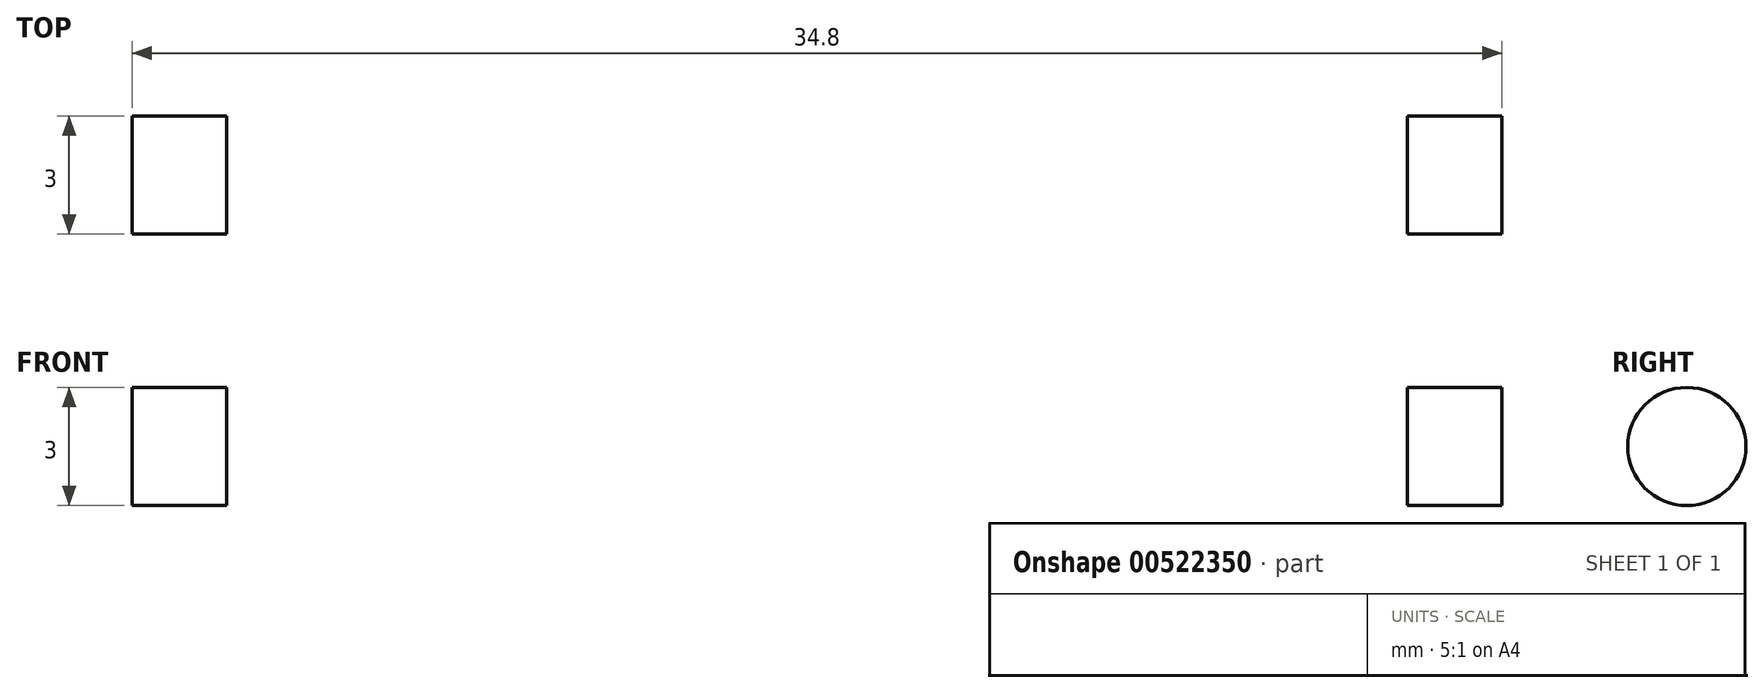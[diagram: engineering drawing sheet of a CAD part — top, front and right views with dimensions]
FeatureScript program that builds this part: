
annotation { "Feature Type Name" : "Feature", "Feature Type Description" : "" }
export const myFeature = defineFeature(function(context is Context, id is Id, definition is map)
    precondition{}
    {
        {
            var Q0;
            Q0=qCreatedBy(makeId("Top.planeOp"),FACE);
            var sketch = newSketch(context, id + "F0", { "sketchPlane" : qUnion([Q0])});
            skLineSegment(sketch, "E0.bottom", {"start": v(15, -21.5) * mm, "end": v(5, -21.5) * mm});
            skLineSegment(sketch, "E0.top", {"start": v(15, 21.5) * mm, "end": v(5, 21.5) * mm});
            skLineSegment(sketch, "E0.left", {"start": v(15, -21.5) * mm, "end": v(15, -5) * mm});
            skLineSegment(sketch, "E0.right", {"start": v(-15, -21.5) * mm, "end": v(-15, -5) * mm});
            skPoint(sketch, "E0.middle", {"position": v(0, 0) * mm});
            skLineSegment(sketch, "E1.bottom", {"start": v(5, -22.7) * mm, "end": v(-5, -22.7) * mm});
            skLineSegment(sketch, "E1.top", {"start": v(5, 22.7) * mm, "end": v(-5, 22.7) * mm});
            skLineSegment(sketch, "E1.left", {"start": v(16.2, -5) * mm, "end": v(16.2, 5) * mm});
            skLineSegment(sketch, "E1.right", {"start": v(-16.2, -5) * mm, "end": v(-16.2, 5) * mm});
            skLineSegment(sketch, "E2.bottom", {"start": v(17.4, -23.9) * mm, "end": v(-17.4, -23.9) * mm});
            skLineSegment(sketch, "E2.top", {"start": v(17.4, 23.9) * mm, "end": v(-17.4, 23.9) * mm});
            skLineSegment(sketch, "E2.left", {"start": v(17.4, -23.9) * mm, "end": v(17.4, 23.9) * mm});
            skLineSegment(sketch, "E2.right", {"start": v(-17.4, -23.9) * mm, "end": v(-17.4, 23.9) * mm});
            skLineSegment(sketch, "E3", {"start": v(-5, -21.5) * mm, "end": v(-5, -22.7) * mm});
            skLineSegment(sketch, "E4", {"start": v(5, -21.5) * mm, "end": v(5, -22.7) * mm});
            skLineSegment(sketch, "E5", {"start": v(0, 0) * mm, "end": v(0, -7.04) * mm, "construction": true});
            skLineSegment(sketch, "E6", {"start": v(-16.2, 5) * mm, "end": v(-15, 5) * mm});
            skLineSegment(sketch, "E7", {"start": v(-16.2, -5) * mm, "end": v(-15, -5) * mm});
            skLineSegment(sketch, "E8", {"start": v(0, 0) * mm, "end": v(8.38, 0) * mm, "construction": true});
            skLineSegment(sketch, "E9", {"start": v(15, 5) * mm, "end": v(16.2, 5) * mm});
            skLineSegment(sketch, "E10", {"start": v(15, -5) * mm, "end": v(16.2, -5) * mm});
            skLineSegment(sketch, "E11", {"start": v(-5, 22.7) * mm, "end": v(-5, 21.5) * mm});
            skLineSegment(sketch, "E12", {"start": v(5, 22.7) * mm, "end": v(5, 21.5) * mm});
            skLineSegment(sketch, "E13.trimOffspring", {"start": v(-5, 21.5) * mm, "end": v(-15, 21.5) * mm});
            skLineSegment(sketch, "E14.trimOffspring", {"start": v(-15, 5) * mm, "end": v(-15, 21.5) * mm});
            skLineSegment(sketch, "E15.trimOffspring", {"start": v(15, 5) * mm, "end": v(15, 21.5) * mm});
            skLineSegment(sketch, "E16.trimOffspring", {"start": v(-5, -21.5) * mm, "end": v(-15, -21.5) * mm});
            skPoint(sketch, "E17.orphan", {"position": v(-16.2, 22.7) * mm});
            skPoint(sketch, "E18.orphan", {"position": v(16.2, 22.7) * mm});
            skPoint(sketch, "E19.orphan", {"position": v(16.2, -22.7) * mm});
            skPoint(sketch, "E20.orphan", {"position": v(-16.2, -22.7) * mm});
            skLineSegment(sketch, "E21", {"start": v(5, 22.7) * mm, "end": v(5, 23.9) * mm});
            skLineSegment(sketch, "E22", {"start": v(-5, 22.7) * mm, "end": v(-5, 23.9) * mm});
            skLineSegment(sketch, "E23", {"start": v(16.2, 5) * mm, "end": v(17.4, 5) * mm});
            skLineSegment(sketch, "E24", {"start": v(16.2, -5) * mm, "end": v(17.4, -5) * mm});
            skLineSegment(sketch, "E25", {"start": v(-16.2, 5) * mm, "end": v(-17.4, 5) * mm});
            skLineSegment(sketch, "E26", {"start": v(-16.2, -5) * mm, "end": v(-17.4, -5) * mm});
            skLineSegment(sketch, "E27", {"start": v(-5, -22.7) * mm, "end": v(-5, -23.9) * mm});
            skLineSegment(sketch, "E28", {"start": v(5, -22.7) * mm, "end": v(5, -23.9) * mm});
            skSolve(sketch);
        }
        {
            var Q0;
            Q0=makeQuery(id+"F0.imprint","IMPRINT",FACE,{"disambiguationData":[TD([[makeQuery(id+"F0.imprint","IMPRINT",EDGE,{"derivedFrom":sQuery(id+"F0.wireOp",EDGE,"E0.bottom")}),1.0]])]});
            var Q1;
            Q1=makeQuery(id+"F0.imprint","IMPRINT",FACE,{"disambiguationData":[TD([[makeQuery(id+"F0.imprint","IMPRINT",EDGE,{"derivedFrom":sQuery(id+"F0.wireOp",EDGE,"E1.left")}),-1.0]])]});
            var Q2;
            Q2=makeQuery(id+"F0.imprint","IMPRINT",FACE,{"disambiguationData":[TD([[makeQuery(id+"F0.imprint","IMPRINT",EDGE,{"derivedFrom":sQuery(id+"F0.wireOp",EDGE,"E0.top")}),-1.0]])]});
            var Q3;
            Q3=makeQuery(id+"F0.imprint","IMPRINT",FACE,{"disambiguationData":[TD([[makeQuery(id+"F0.imprint","IMPRINT",EDGE,{"derivedFrom":sQuery(id+"F0.wireOp",EDGE,"E1.top")}),-1.0]])]});
            var Q4;
            Q4=makeQuery(id+"F0.imprint","IMPRINT",FACE,{"disambiguationData":[TD([[makeQuery(id+"F0.imprint","IMPRINT",EDGE,{"derivedFrom":sQuery(id+"F0.wireOp",EDGE,"E6")}),1.0]])]});
            var Q5;
            Q5=makeQuery(id+"F0.imprint","IMPRINT",FACE,{"disambiguationData":[TD([[makeQuery(id+"F0.imprint","IMPRINT",EDGE,{"derivedFrom":sQuery(id+"F0.wireOp",EDGE,"E0.right")}),1.0]])]});
            var Q6;
            Q6=makeQuery(id+"F0.imprint","IMPRINT",FACE,{"disambiguationData":[TD([[makeQuery(id+"F0.imprint","IMPRINT",EDGE,{"derivedFrom":sQuery(id+"F0.wireOp",EDGE,"E1.bottom")}),1.0]])]});
            var Q7;
            Q7=makeQuery(id+"F0.imprint","IMPRINT",FACE,{"disambiguationData":[TD([[makeQuery(id+"F0.imprint","IMPRINT",EDGE,{"derivedFrom":sQuery(id+"F0.wireOp",EDGE,"E1.right")}),1.0]])]});
            extrude(context, id + "F1", {"entities" : qUnion([Q0, Q1, Q2, Q3, Q4, Q5, Q6, Q7]), "depth" : 30 * mm, "offsetDistance" : 25 * mm});
        }
        {
            var Q0;
            Q0=makeQuery(id+"F1.opExtrude","SWEPT_FACE",FACE,{"disambiguationData":[OSD([sQuery(id+"F0.wireOp",EDGE,"E2.bottom")])]});
            var sketch = newSketch(context, id + "F2", { "sketchPlane" : qUnion([Q0])});
            skLineSegment(sketch, "E29.bottom", {"start": v(-5, 24) * mm, "end": v(5, 24) * mm});
            skLineSegment(sketch, "E29.top", {"start": v(-5, 20) * mm, "end": v(5, 20) * mm});
            skLineSegment(sketch, "E29.left", {"start": v(-5, 24) * mm, "end": v(-5, 20) * mm});
            skLineSegment(sketch, "E29.right", {"start": v(5, 24) * mm, "end": v(5, 20) * mm});
            skLineSegment(sketch, "E30", {"start": v(0, 30) * mm, "end": v(0, 0) * mm, "construction": true});
            skLineSegment(sketch, "E31.bottom", {"start": v(-5, 10) * mm, "end": v(5, 10) * mm});
            skLineSegment(sketch, "E31.top", {"start": v(-5, 6) * mm, "end": v(5, 6) * mm});
            skLineSegment(sketch, "E31.left", {"start": v(-5, 10) * mm, "end": v(-5, 6) * mm});
            skLineSegment(sketch, "E31.right", {"start": v(5, 10) * mm, "end": v(5, 6) * mm});
            skCircle(sketch, "E32", {"center": v(0, 15) * mm, "radius": 1.5 * mm});
            skSolve(sketch);
        }
        {
            var Q0;
            Q0=makeQuery(id+"F2.imprint","IMPRINT",FACE,{"disambiguationData":[TD([[makeQuery(id+"F2.imprint","IMPRINT",EDGE,{"derivedFrom":sQuery(id+"F2.wireOp",EDGE,"E29.bottom")}),-1.0]])]});
            var Q1;
            Q1=makeQuery(id+"F2.imprint","IMPRINT",FACE,{"disambiguationData":[TD([[makeQuery(id+"F2.imprint","IMPRINT",EDGE,{"derivedFrom":sQuery(id+"F2.wireOp",EDGE,"E31.bottom")}),-1.0]])]});
            extrude(context, id + "F3", {"entities" : qUnion([Q0, Q1]), "operationType" : NewBodyOperationType.REMOVE, "endBound" : BoundingType.THROUGH_ALL, "oppositeDirection" : true, "depth" : 53.6 * mm, "offsetDistance" : 25 * mm});
        }
        {
            var Q0;
            Q0=makeQuery(id+"F1.opExtrude","SWEPT_FACE",FACE,{"disambiguationData":[OSD([sQuery(id+"F0.wireOp",EDGE,"E2.right")])]});
            var sketch = newSketch(context, id + "F4", { "sketchPlane" : qUnion([Q0])});
            skLineSegment(sketch, "E33", {"start": v(0, 30) * mm, "end": v(0, 0) * mm, "construction": true});
            skLineSegment(sketch, "E34.bottom", {"start": v(-5, 24) * mm, "end": v(5, 24) * mm});
            skLineSegment(sketch, "E34.top", {"start": v(-5, 20) * mm, "end": v(5, 20) * mm});
            skLineSegment(sketch, "E34.left", {"start": v(-5, 24) * mm, "end": v(-5, 20) * mm});
            skLineSegment(sketch, "E34.right", {"start": v(5, 24) * mm, "end": v(5, 20) * mm});
            skLineSegment(sketch, "E35.bottom", {"start": v(-5, 10) * mm, "end": v(5, 10) * mm});
            skLineSegment(sketch, "E35.top", {"start": v(-5, 6) * mm, "end": v(5, 6) * mm});
            skLineSegment(sketch, "E35.left", {"start": v(-5, 10) * mm, "end": v(-5, 6) * mm});
            skLineSegment(sketch, "E35.right", {"start": v(5, 10) * mm, "end": v(5, 6) * mm});
            skCircle(sketch, "E36", {"center": v(-15, 10) * mm, "radius": 1.5 * mm});
            skCircle(sketch, "E37.MirrorC", {"center": v(15, 10) * mm, "radius": 1.5 * mm});
            skSolve(sketch);
        }
        {
            var Q0;
            Q0=makeQuery(id+"F4.imprint","IMPRINT",FACE,{"disambiguationData":[TD([[makeQuery(id+"F4.imprint","IMPRINT",EDGE,{"derivedFrom":sQuery(id+"F4.wireOp",EDGE,"E34.bottom")}),-1.0]])]});
            var Q1;
            Q1=makeQuery(id+"F4.imprint","IMPRINT",FACE,{"disambiguationData":[TD([[makeQuery(id+"F4.imprint","IMPRINT",EDGE,{"derivedFrom":sQuery(id+"F4.wireOp",EDGE,"E35.bottom")}),-1.0]])]});
            extrude(context, id + "F5", {"entities" : qUnion([Q0, Q1]), "operationType" : NewBodyOperationType.REMOVE, "endBound" : BoundingType.THROUGH_ALL, "oppositeDirection" : true, "depth" : 25 * mm, "offsetDistance" : 25 * mm});
        }
        {
            var Q0;
            Q0=makeQuery(id+"F1.opExtrude","CAP_FACE",FACE,{"disambiguationData":[OSD([sQuery(id+"F0.wireOp",EDGE,"E0.bottom"),sQuery(id+"F0.wireOp",EDGE,"E0.top"),sQuery(id+"F0.wireOp",EDGE,"E0.left"),sQuery(id+"F0.wireOp",EDGE,"E0.right"),sQuery(id+"F0.wireOp",EDGE,"E1.bottom"),sQuery(id+"F0.wireOp",EDGE,"E1.top"),sQuery(id+"F0.wireOp",EDGE,"E1.left"),sQuery(id+"F0.wireOp",EDGE,"E1.right"),sQuery(id+"F0.wireOp",EDGE,"E2.bottom"),sQuery(id+"F0.wireOp",EDGE,"E2.top"),sQuery(id+"F0.wireOp",EDGE,"E2.left"),sQuery(id+"F0.wireOp",EDGE,"E2.right"),sQuery(id+"F0.wireOp",EDGE,"E3"),sQuery(id+"F0.wireOp",EDGE,"E4"),sQuery(id+"F0.wireOp",EDGE,"E6"),sQuery(id+"F0.wireOp",EDGE,"E7"),sQuery(id+"F0.wireOp",EDGE,"E9"),sQuery(id+"F0.wireOp",EDGE,"E10"),sQuery(id+"F0.wireOp",EDGE,"E11"),sQuery(id+"F0.wireOp",EDGE,"E12"),sQuery(id+"F0.wireOp",EDGE,"E13.trimOffspring"),sQuery(id+"F0.wireOp",EDGE,"E14.trimOffspring"),sQuery(id+"F0.wireOp",EDGE,"E15.trimOffspring"),sQuery(id+"F0.wireOp",EDGE,"E16.trimOffspring")])],"isStart":false});
            var sketch = newSketch(context, id + "F6", { "sketchPlane" : qUnion([Q0])});
            skLineSegment(sketch, "E38", {"start": v(5, 22.7) * mm, "end": v(5, 23.9) * mm});
            skLineSegment(sketch, "E39", {"start": v(-5, 22.7) * mm, "end": v(-5, 23.9) * mm});
            skLineSegment(sketch, "E40", {"start": v(16.2, 5) * mm, "end": v(17.4, 5) * mm});
            skLineSegment(sketch, "E41", {"start": v(16.2, -5) * mm, "end": v(17.4, -5) * mm});
            skLineSegment(sketch, "E42", {"start": v(5, -22.7) * mm, "end": v(5, -23.9) * mm});
            skLineSegment(sketch, "E43", {"start": v(-5, -22.7) * mm, "end": v(-5, -23.9) * mm});
            skLineSegment(sketch, "E44", {"start": v(-16.2, 5) * mm, "end": v(-17.4, 5) * mm});
            skLineSegment(sketch, "E45", {"start": v(-16.2, -5) * mm, "end": v(-17.4, -5) * mm});
            skSolve(sketch);
        }
        {
            var Q0;
            {var subQ0=sQuery(id+"F6.wireOp",EDGE,"E38");Q0=makeQuery(id+"F6.imprint","IMPRINT",FACE,{"disambiguationData":[TD([[makeQuery(id+"F6.imprint","IMPRINT",EDGE,{"derivedFrom":subQ0}),1.0]])]});}
            var Q1;
            {var subQ0=sQuery(id+"F6.wireOp",EDGE,"E40");Q1=makeQuery(id+"F6.imprint","IMPRINT",FACE,{"disambiguationData":[TD([[makeQuery(id+"F6.imprint","IMPRINT",EDGE,{"derivedFrom":subQ0}),-1.0]])]});}
            var Q2;
            {var subQ0=sQuery(id+"F6.wireOp",EDGE,"E44");Q2=makeQuery(id+"F6.imprint","IMPRINT",FACE,{"disambiguationData":[TD([[makeQuery(id+"F6.imprint","IMPRINT",EDGE,{"derivedFrom":subQ0}),1.0]])]});}
            var Q3;
            {var subQ0=sQuery(id+"F6.wireOp",EDGE,"E42");Q3=makeQuery(id+"F6.imprint","IMPRINT",FACE,{"disambiguationData":[TD([[makeQuery(id+"F6.imprint","IMPRINT",EDGE,{"derivedFrom":subQ0}),-1.0]])]});}
            extrude(context, id + "F7", {"entities" : qUnion([Q0, Q1, Q2, Q3]), "operationType" : NewBodyOperationType.REMOVE, "oppositeDirection" : true, "depth" : 2.4 * mm, "offsetDistance" : 25 * mm});
        }
        {
            var Q0;
            Q0=makeQuery(id+"F0.imprint","IMPRINT",FACE,{"disambiguationData":[TD([[makeQuery(id+"F0.imprint","IMPRINT",EDGE,{"derivedFrom":sQuery(id+"F0.wireOp",EDGE,"E1.left")}),-1.0]])]});
            var Q1;
            Q1=makeQuery(id+"F0.imprint","IMPRINT",FACE,{"disambiguationData":[TD([[makeQuery(id+"F0.imprint","IMPRINT",EDGE,{"derivedFrom":sQuery(id+"F0.wireOp",EDGE,"E1.top")}),-1.0]])]});
            var Q2;
            Q2=makeQuery(id+"F0.imprint","IMPRINT",FACE,{"disambiguationData":[TD([[makeQuery(id+"F0.imprint","IMPRINT",EDGE,{"derivedFrom":sQuery(id+"F0.wireOp",EDGE,"E1.bottom")}),1.0]])]});
            var Q3;
            Q3=makeQuery(id+"F0.imprint","IMPRINT",FACE,{"disambiguationData":[TD([[makeQuery(id+"F0.imprint","IMPRINT",EDGE,{"derivedFrom":sQuery(id+"F0.wireOp",EDGE,"E1.right")}),1.0]])]});
            extrude(context, id + "F8", {"entities" : qUnion([Q0, Q1, Q2, Q3]), "operationType" : NewBodyOperationType.REMOVE, "depth" : 2.4 * mm, "offsetDistance" : 25 * mm});
        }
        {
            var Q0;
            Q0=makeQuery(id+"F1.opExtrude","SWEPT_EDGE",EDGE,{"disambiguationData":[OSD([sQuery(id+"F0.wireOp",EDGE,"E2.bottom"),sQuery(id+"F0.wireOp",EDGE,"E2.right")])]});
            var Q1;
            Q1=makeQuery(id+"F1.opExtrude","SWEPT_EDGE",EDGE,{"disambiguationData":[OSD([sQuery(id+"F0.wireOp",EDGE,"E2.top"),sQuery(id+"F0.wireOp",EDGE,"E2.right")])]});
            var Q2;
            Q2=makeQuery(id+"F1.opExtrude","SWEPT_EDGE",EDGE,{"disambiguationData":[OSD([sQuery(id+"F0.wireOp",EDGE,"E2.bottom"),sQuery(id+"F0.wireOp",EDGE,"E2.left")])]});
            var Q3;
            Q3=makeQuery(id+"F1.opExtrude","SWEPT_EDGE",EDGE,{"disambiguationData":[OSD([sQuery(id+"F0.wireOp",EDGE,"E2.top"),sQuery(id+"F0.wireOp",EDGE,"E2.left")])]});
            fillet(context, id + "F9", {"entities" : qUnion([Q0, Q1, Q2, Q3]), "radius" : 5 * mm, "tangentPropagation" : true, "allowEdgeOverflow" : false});
        }
        {
            var Q0;
            Q0=makeQuery(id+"F2.imprint","IMPRINT",FACE,{"disambiguationData":[TD([[makeQuery(id+"F2.imprint","IMPRINT",EDGE,{"derivedFrom":sQuery(id+"F2.wireOp",EDGE,"E32")}),1.0]])]});
            extrude(context, id + "F10", {"entities" : qUnion([Q0]), "operationType" : NewBodyOperationType.REMOVE, "endBound" : BoundingType.UP_TO_NEXT, "oppositeDirection" : true, "depth" : 6 * mm, "offsetDistance" : 25 * mm});
        }
        {
            var Q0;
            Q0=makeQuery(id+"F1.opExtrude","SWEPT_FACE",FACE,{"disambiguationData":[OSD([sQuery(id+"F0.wireOp",EDGE,"E2.top")])]});
            var sketch = newSketch(context, id + "F11", { "sketchPlane" : qUnion([Q0])});
            skLineSegment(sketch, "E46", {"start": v(-5, 20) * mm, "end": v(5, 10) * mm, "construction": true});
            skCircle(sketch, "E47", {"center": v(0, 15) * mm, "radius": 2.5 * mm});
            skSolve(sketch);
        }
        {
            var Q0;
            Q0=makeQuery(id+"F11.imprint","IMPRINT",FACE,{"disambiguationData":[TD([[makeQuery(id+"F11.imprint","IMPRINT",EDGE,{"derivedFrom":sQuery(id+"F11.wireOp",EDGE,"E47")}),1.0]])]});
            extrude(context, id + "F12", {"entities" : qUnion([Q0]), "operationType" : NewBodyOperationType.REMOVE, "endBound" : BoundingType.UP_TO_NEXT, "oppositeDirection" : true, "depth" : 7.6 * mm, "offsetDistance" : 25 * mm});
        }
        {
            var Q0;
            Q0=makeQuery(id+"F4.imprint","IMPRINT",FACE,{"disambiguationData":[TD([[makeQuery(id+"F4.imprint","IMPRINT",EDGE,{"derivedFrom":sQuery(id+"F4.wireOp",EDGE,"E36")}),1.0]])]});
            var Q1;
            Q1=makeQuery(id+"F4.imprint","IMPRINT",FACE,{"disambiguationData":[TD([[makeQuery(id+"F4.imprint","IMPRINT",EDGE,{"derivedFrom":sQuery(id+"F4.wireOp",EDGE,"E37.MirrorC")}),-1.0]])]});
            extrude(context, id + "F13", {"entities" : qUnion([Q0, Q1]), "operationType" : NewBodyOperationType.REMOVE, "endBound" : BoundingType.THROUGH_ALL, "oppositeDirection" : true, "depth" : 25 * mm, "offsetDistance" : 25 * mm});
        }
    });
